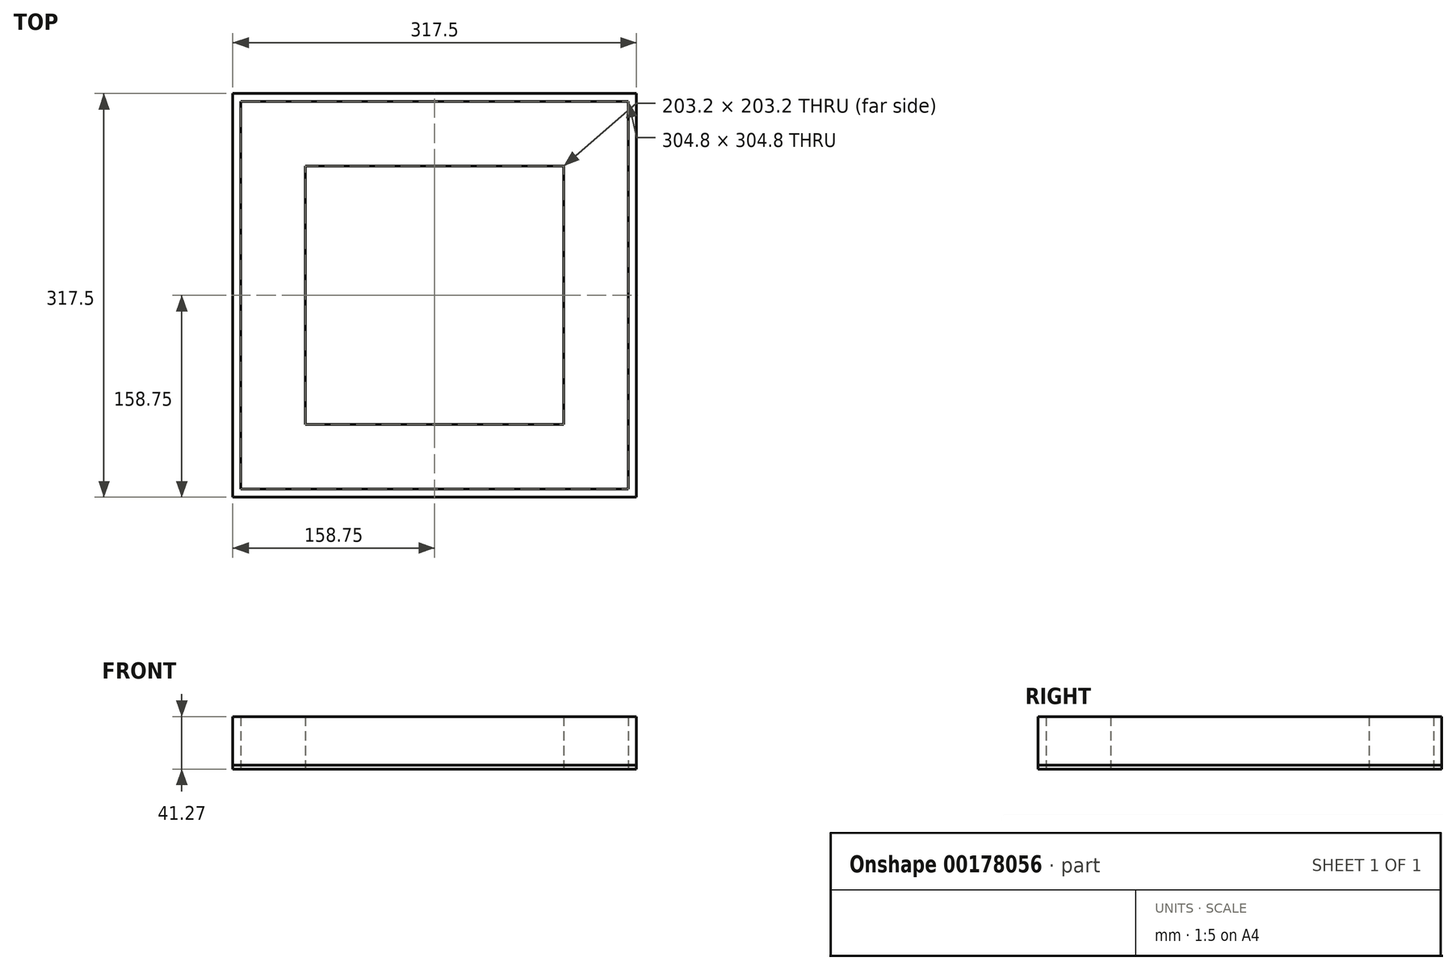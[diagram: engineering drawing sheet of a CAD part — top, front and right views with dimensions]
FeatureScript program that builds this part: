
annotation { "Feature Type Name" : "Feature", "Feature Type Description" : "" }
export const myFeature = defineFeature(function(context is Context, id is Id, definition is map)
    precondition{}
    {
        {
            var Q0;
            Q0=qCreatedBy(makeId("Top.planeOp"),FACE);
            var sketch = newSketch(context, id + "F0", { "sketchPlane" : qUnion([Q0])});
            skLineSegment(sketch, "E0.bottom", {"start": v(0, 0) * mm, "end": v(304.8, 0) * mm});
            skLineSegment(sketch, "E0.top", {"start": v(0, 304.8) * mm, "end": v(304.8, 304.8) * mm});
            skLineSegment(sketch, "E0.left", {"start": v(0, 0) * mm, "end": v(0, 304.8) * mm});
            skLineSegment(sketch, "E0.right", {"start": v(304.8, 0) * mm, "end": v(304.8, 304.8) * mm});
            skLineSegment(sketch, "E1.bottom", {"start": v(50.8, 50.8) * mm, "end": v(254, 50.8) * mm});
            skLineSegment(sketch, "E1.top", {"start": v(50.8, 254) * mm, "end": v(254, 254) * mm});
            skLineSegment(sketch, "E1.left", {"start": v(50.8, 50.8) * mm, "end": v(50.8, 254) * mm});
            skLineSegment(sketch, "E1.right", {"start": v(254, 50.8) * mm, "end": v(254, 254) * mm});
            skLineSegment(sketch, "E2.bottom", {"start": v(-6.35, 311.15) * mm, "end": v(311.15, 311.15) * mm});
            skLineSegment(sketch, "E2.top", {"start": v(-6.35, -6.35) * mm, "end": v(311.15, -6.35) * mm});
            skLineSegment(sketch, "E2.left", {"start": v(-6.35, 311.15) * mm, "end": v(-6.35, -6.35) * mm});
            skLineSegment(sketch, "E2.right", {"start": v(311.15, 311.15) * mm, "end": v(311.15, -6.35) * mm});
            skSolve(sketch);
        }
        {
            var Q0;
            Q0=makeQuery(id+"F0.imprint","IMPRINT",FACE,{"disambiguationData":[TD([[makeQuery(id+"F0.imprint","IMPRINT",EDGE,{"derivedFrom":sQuery(id+"F0.wireOp",EDGE,"E1.bottom")}),1.0]])]});
            var Q1;
            Q1=makeQuery(id+"F0.imprint","IMPRINT",FACE,{"disambiguationData":[TD([[makeQuery(id+"F0.imprint","IMPRINT",EDGE,{"derivedFrom":sQuery(id+"F0.wireOp",EDGE,"E0.bottom")}),-1.0]])]});
            extrude(context, id + "F1", {"entities" : qUnion([Q0, Q1]), "depth" : 41.27 * mm});
        }
        {
            var Q0;
            Q0 = qSketchRegion(id + "F0", true);
            var Q1;
            Q1=makeQuery(id+"F0.imprint","IMPRINT",FACE,{"disambiguationData":[TD([[makeQuery(id+"F0.imprint","IMPRINT",EDGE,{"derivedFrom":sQuery(id+"F0.wireOp",EDGE,"E0.bottom")}),1.0]])]});
            extrude(context, id + "F2", {"entities" : qUnion([Q0, Q1]), "depth" : 3.17 * mm});
        }
    });
